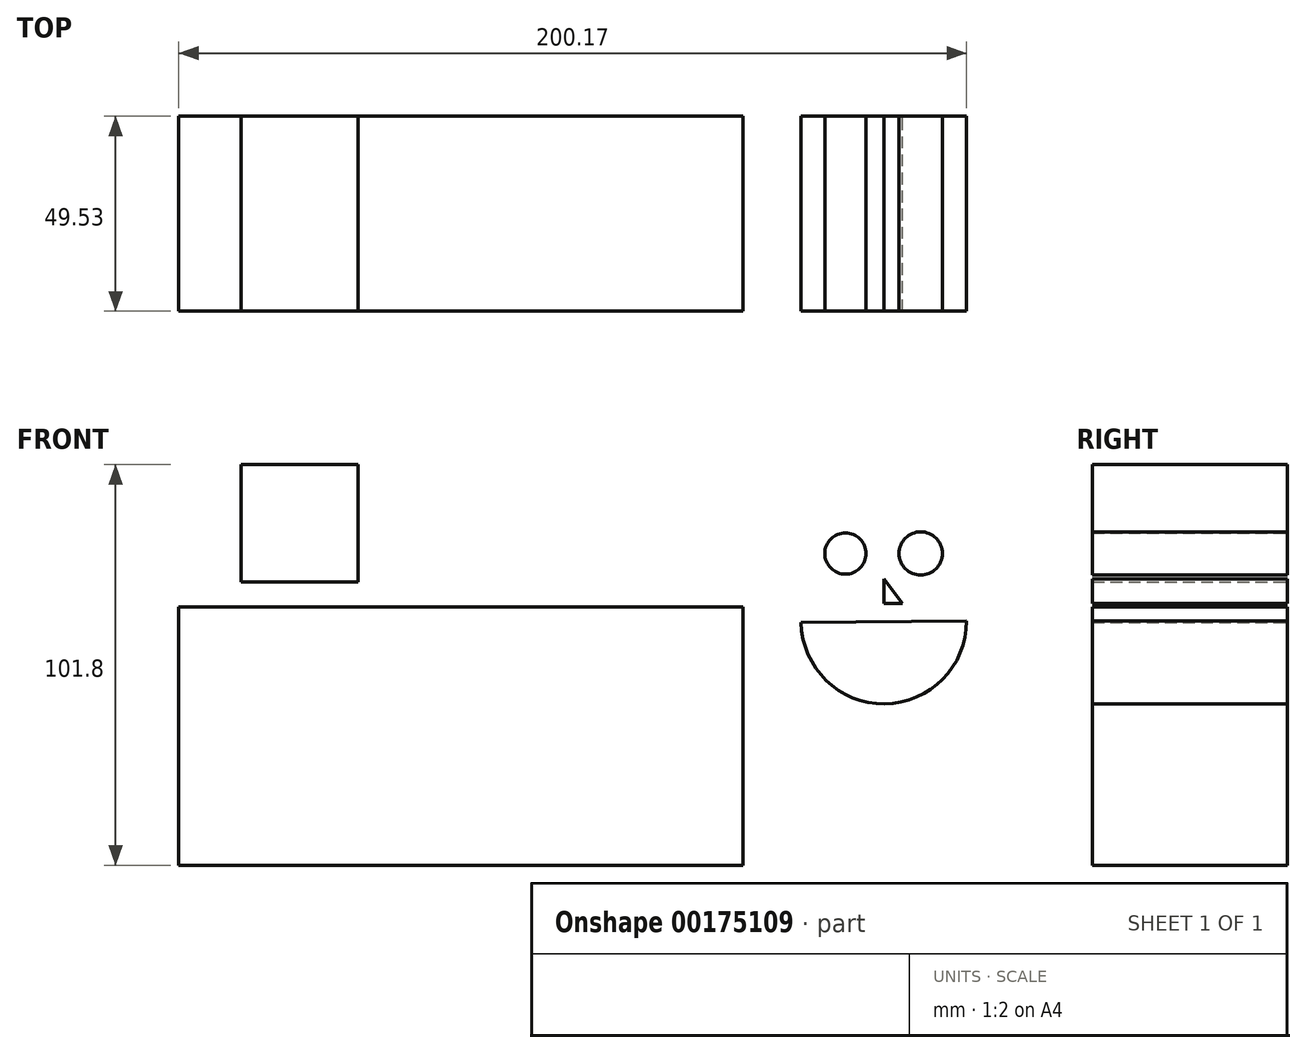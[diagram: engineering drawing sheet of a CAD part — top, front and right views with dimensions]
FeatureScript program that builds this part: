
annotation { "Feature Type Name" : "Feature", "Feature Type Description" : "" }
export const myFeature = defineFeature(function(context is Context, id is Id, definition is map)
    precondition{}
    {
        {
            var Q0;
            Q0=qCreatedBy(makeId("Front.planeOp"),FACE);
            var sketch = newSketch(context, id + "F0", { "sketchPlane" : qUnion([Q0])});
            skLineSegment(sketch, "E0.bottom", {"start": v(-71.67, 32.82) * mm, "end": v(71.67, 32.82) * mm});
            skLineSegment(sketch, "E0.top", {"start": v(-71.67, -32.82) * mm, "end": v(71.67, -32.82) * mm});
            skLineSegment(sketch, "E0.left", {"start": v(-71.67, 32.82) * mm, "end": v(-71.67, -32.82) * mm});
            skLineSegment(sketch, "E0.right", {"start": v(71.67, 32.82) * mm, "end": v(71.67, -32.82) * mm});
            skPoint(sketch, "E0.middle", {"position": v(0, 0) * mm});
            skLineSegment(sketch, "E1.bottom", {"start": v(-26.04, 39.18) * mm, "end": v(-55.84, 39.18) * mm});
            skLineSegment(sketch, "E1.top", {"start": v(-26.04, 68.98) * mm, "end": v(-55.84, 68.98) * mm});
            skLineSegment(sketch, "E1.left", {"start": v(-26.04, 39.18) * mm, "end": v(-26.04, 68.98) * mm});
            skLineSegment(sketch, "E1.right", {"start": v(-55.84, 39.18) * mm, "end": v(-55.84, 68.98) * mm});
            skPoint(sketch, "E1.middle", {"position": v(-40.94, 54.08) * mm});
            skSolve(sketch);
        }
        {
            var Q0;
            Q0=makeQuery(id+"F0.imprint","IMPRINT",FACE,{"disambiguationData":[TD([[makeQuery(id+"F0.imprint","IMPRINT",EDGE,{"derivedFrom":sQuery(id+"F0.wireOp",EDGE,"E1.bottom")}),-1.0]])]});
            var sketch = newSketch(context, id + "F1", { "sketchPlane" : qUnion([Q0])});
            skCircle(sketch, "E2", {"center": v(97.73, 46.4) * mm, "radius": 5.25 * mm});
            skCircle(sketch, "E3", {"center": v(116.85, 46.41) * mm, "radius": 5.5 * mm});
            skArc(sketch, "E4", {"start": v(86.46, 28.82) * mm, "mid": v(107.68, 8.2) * mm, "end": v(128.5, 29.23) * mm});
            skLineSegment(sketch, "E5", {"start": v(107.48, 39.96) * mm, "end": v(107.48, 33.71) * mm});
            skLineSegment(sketch, "E6", {"start": v(107.48, 33.71) * mm, "end": v(112.16, 33.71) * mm});
            skPoint(sketch, "E7", {"position": v(107.48, 36.84) * mm});
            skLineSegment(sketch, "E8", {"start": v(128.5, 29.23) * mm, "end": v(86.46, 28.82) * mm});
            skLineSegment(sketch, "E9", {"start": v(107.48, 39.96) * mm, "end": v(112.16, 33.71) * mm});
            skSolve(sketch);
        }
        {
            var Q0;
            Q0=makeQuery(id+"F1.imprint","IMPRINT",FACE,{"disambiguationData":[TD([[makeQuery(id+"F1.imprint","IMPRINT",EDGE,{"derivedFrom":sQuery(id+"F1.wireOp",EDGE,"E2")}),1.0]])]});
            var Q1;
            Q1=makeQuery(id+"F1.imprint","IMPRINT",FACE,{"disambiguationData":[TD([[makeQuery(id+"F1.imprint","IMPRINT",EDGE,{"derivedFrom":sQuery(id+"F1.wireOp",EDGE,"E3")}),1.0]])]});
            var Q2;
            Q2=makeQuery(id+"F1.imprint","IMPRINT",FACE,{"disambiguationData":[TD([[makeQuery(id+"F1.imprint","IMPRINT",EDGE,{"derivedFrom":sQuery(id+"F1.wireOp",EDGE,"E5")}),1.0]])]});
            var Q3;
            Q3=makeQuery(id+"F1.imprint","IMPRINT",FACE,{"disambiguationData":[TD([[makeQuery(id+"F1.imprint","IMPRINT",EDGE,{"derivedFrom":sQuery(id+"F1.wireOp",EDGE,"E4")}),1.0]])]});
            var Q4;
            Q4=makeQuery(id+"F0.imprint","IMPRINT",FACE,{"disambiguationData":[TD([[makeQuery(id+"F0.imprint","IMPRINT",EDGE,{"derivedFrom":sQuery(id+"F0.wireOp",EDGE,"E0.bottom")}),-1.0]])]});
            var Q5;
            Q5=makeQuery(id+"F0.imprint","IMPRINT",FACE,{"disambiguationData":[TD([[makeQuery(id+"F0.imprint","IMPRINT",EDGE,{"derivedFrom":sQuery(id+"F0.wireOp",EDGE,"E1.bottom")}),-1.0]])]});
            extrude(context, id + "F2", {"entities" : qUnion([Q0, Q1, Q2, Q3, Q4, Q5]), "depth" : 49.53 * mm});
        }
    });
